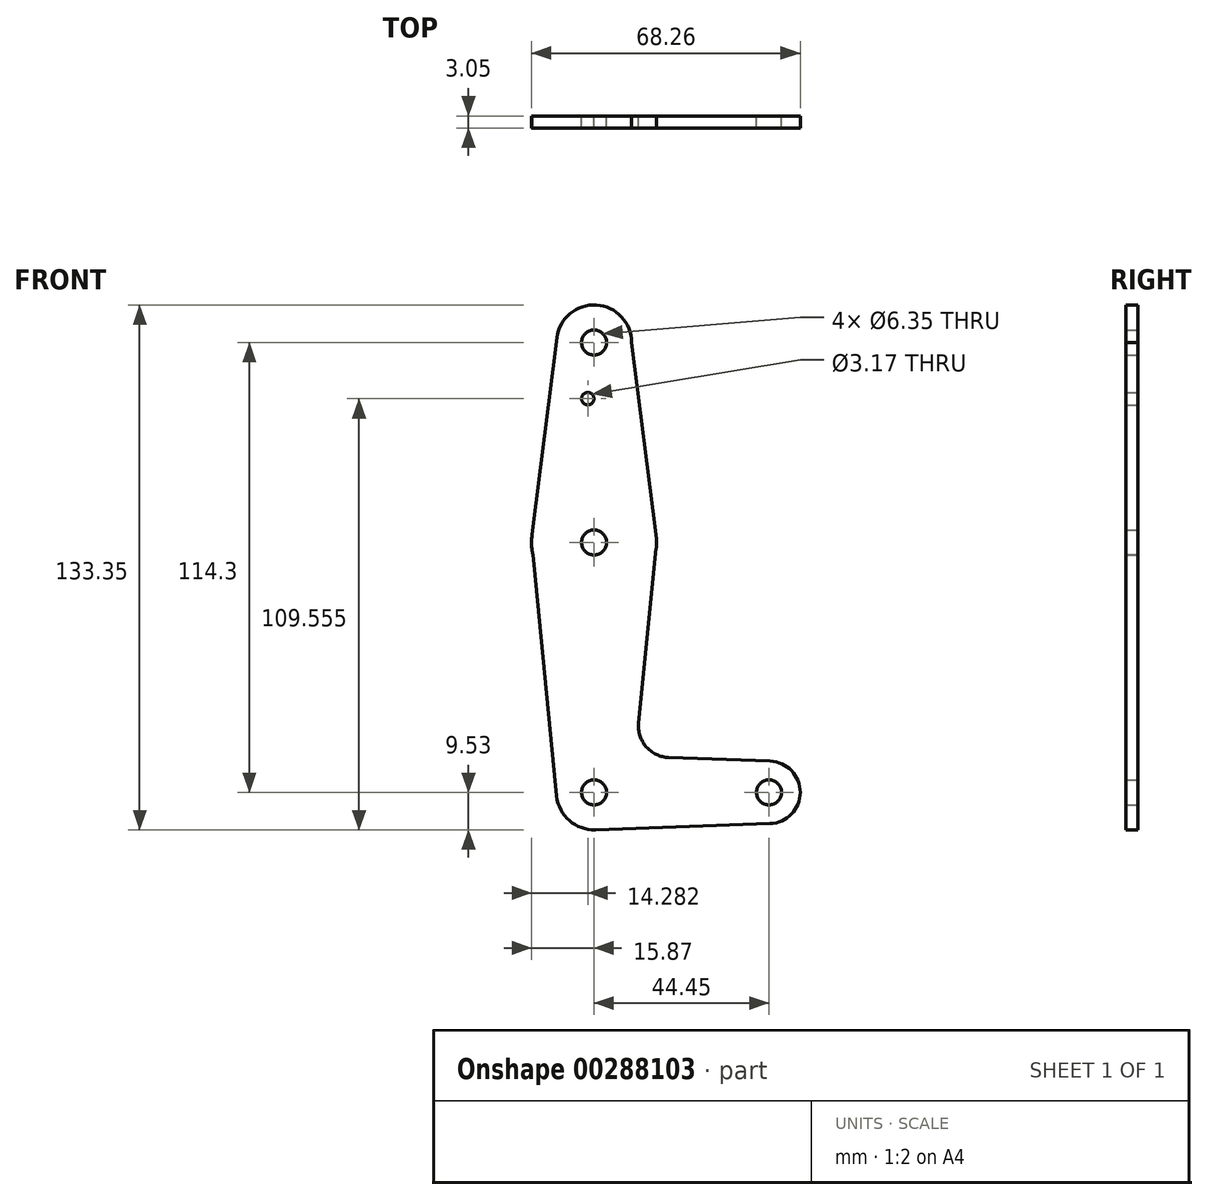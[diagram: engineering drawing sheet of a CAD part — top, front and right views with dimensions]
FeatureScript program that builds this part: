
annotation { "Feature Type Name" : "Feature", "Feature Type Description" : "" }
export const myFeature = defineFeature(function(context is Context, id is Id, definition is map)
    precondition{}
    {
        {
            var Q0;
            Q0=qCreatedBy(makeId("Front.planeOp"),FACE);
            var sketch = newSketch(context, id + "F0", { "sketchPlane" : qUnion([Q0])});
            skLineSegment(sketch, "E0", {"start": v(0, 50.8) * mm, "end": v(0, -63.5) * mm, "construction": true});
            skLineSegment(sketch, "E1", {"start": v(0, -63.5) * mm, "end": v(44.45, -63.5) * mm, "construction": true});
            skCircle(sketch, "E2", {"center": v(0, 50.8) * mm, "radius": 9.53 * mm});
            skCircle(sketch, "E3", {"center": v(0, 0) * mm, "radius": 15.88 * mm});
            skCircle(sketch, "E4", {"center": v(0, -63.5) * mm, "radius": 9.53 * mm});
            skCircle(sketch, "E5", {"center": v(44.45, -63.5) * mm, "radius": 7.94 * mm});
            skLineSegment(sketch, "E6", {"start": v(-9.45, 52) * mm, "end": v(-15.75, 2) * mm});
            skLineSegment(sketch, "E7", {"start": v(9.52, 50.8) * mm, "end": v(15.75, 2) * mm});
            skLineSegment(sketch, "E8", {"start": v(-15.88, 0) * mm, "end": v(-9.48, -64.44) * mm});
            skCircle(sketch, "E9", {"center": v(0, 50.8) * mm, "radius": 3.18 * mm});
            skCircle(sketch, "E10", {"center": v(0, 0) * mm, "radius": 3.18 * mm});
            skCircle(sketch, "E11", {"center": v(0, -63.5) * mm, "radius": 3.18 * mm});
            skCircle(sketch, "E12", {"center": v(44.45, -63.5) * mm, "radius": 3.18 * mm});
            skCircle(sketch, "E13", {"center": v(-1.59, 36.53) * mm, "radius": 1.59 * mm});
            skLineSegment(sketch, "E14", {"start": v(0.34, -73.02) * mm, "end": v(44.73, -71.43) * mm});
            skLineSegment(sketch, "E15", {"start": v(15.8, -1.59) * mm, "end": v(11.34, -45.9) * mm});
            skLineSegment(sketch, "E16", {"start": v(18.97, -54.65) * mm, "end": v(44.73, -55.57) * mm});
            skArc(sketch, "E17.filletArc", {"start": v(11.34, -45.9) * mm, "mid": v(13.26, -51.93) * mm, "end": v(18.97, -54.65) * mm});
            skSolve(sketch);
        }
        {
            var Q0;
            Q0=qSketchRegion(id+"F0",true);
            extrude(context, id + "F1", {"entities" : qUnion([Q0]), "depth" : 3.05 * mm});
        }
    });
